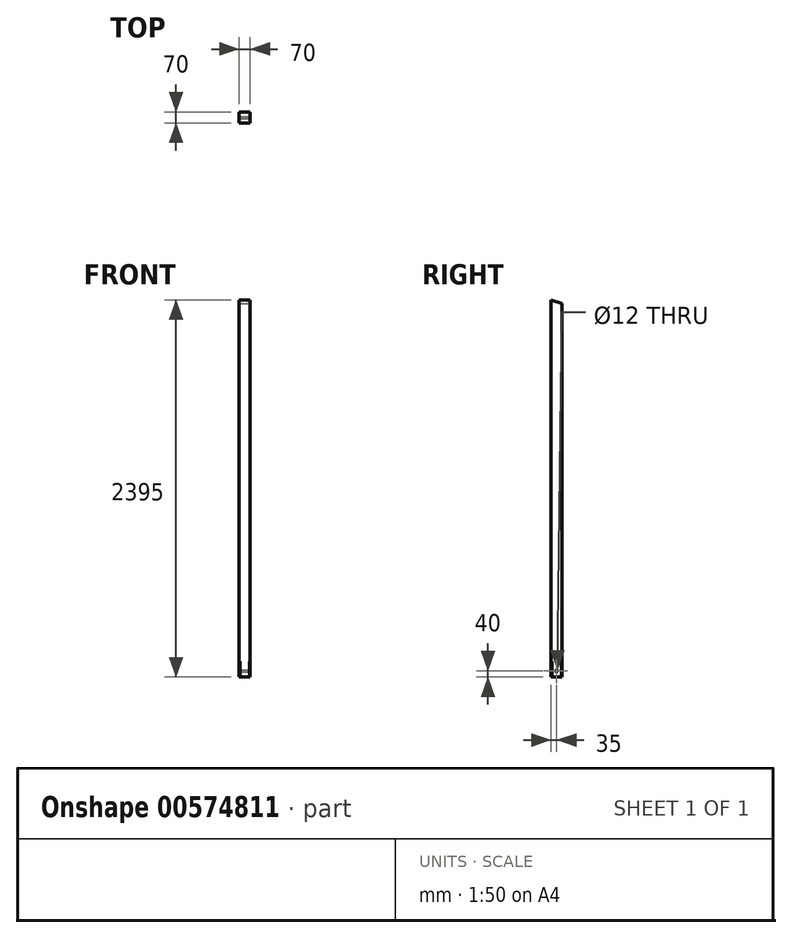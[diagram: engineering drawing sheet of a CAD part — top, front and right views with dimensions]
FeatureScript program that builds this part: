
annotation { "Feature Type Name" : "Feature", "Feature Type Description" : "" }
export const myFeature = defineFeature(function(context is Context, id is Id, definition is map)
    precondition{}
    {
        {
            var Q0;
            Q0=qCreatedBy(makeId("Top.planeOp"),FACE);
            var sketch = newSketch(context, id + "F0", { "sketchPlane" : qUnion([Q0])});
            skLineSegment(sketch, "E0.bottom", {"start": v(-35, -35) * mm, "end": v(35, -35) * mm});
            skLineSegment(sketch, "E0.top", {"start": v(-35, 35) * mm, "end": v(35, 35) * mm});
            skLineSegment(sketch, "E0.left", {"start": v(-35, -35) * mm, "end": v(-35, 35) * mm});
            skLineSegment(sketch, "E0.right", {"start": v(35, -35) * mm, "end": v(35, 35) * mm});
            skSolve(sketch);
        }
        {
            var Q0;
            Q0=makeQuery(id+"F0.imprint","IMPRINT",FACE,{"disambiguationData":[TD([[makeQuery(id+"F0.imprint","IMPRINT",EDGE,{"derivedFrom":sQuery(id+"F0.wireOp",EDGE,"E0.bottom")}),1.0]])]});
            extrude(context, id + "F1", {"entities" : qUnion([Q0]), "depth" : 100 * mm, "offsetDistance" : 25 * mm});
        }
        {
            var Q0;
            Q0=makeQuery(id+"F1.opExtrude","SWEPT_EDGE",EDGE,{"disambiguationData":[OSD([sQuery(id+"F0.wireOp",EDGE,"E0.bottom"),sQuery(id+"F0.wireOp",EDGE,"E0.left")])]});
            var Q1;
            Q1=makeQuery(id+"F1.opExtrude","SWEPT_EDGE",EDGE,{"disambiguationData":[OSD([sQuery(id+"F0.wireOp",EDGE,"E0.bottom"),sQuery(id+"F0.wireOp",EDGE,"E0.right")])]});
            var Q2;
            Q2=makeQuery(id+"F1.opExtrude","SWEPT_EDGE",EDGE,{"disambiguationData":[OSD([sQuery(id+"F0.wireOp",EDGE,"E0.top"),sQuery(id+"F0.wireOp",EDGE,"E0.right")])]});
            var Q3;
            Q3=makeQuery(id+"F1.opExtrude","SWEPT_EDGE",EDGE,{"disambiguationData":[OSD([sQuery(id+"F0.wireOp",EDGE,"E0.top"),sQuery(id+"F0.wireOp",EDGE,"E0.left")])]});
            chamfer(context, id + "F2", {"entities" : qUnion([Q0, Q1, Q2, Q3]), "width" : 5 * mm, "tangentPropagation" : true});
        }
        {
            var Q0;
            Q0=makeQuery(id+"F1.opExtrude","CAP_FACE",FACE,{"disambiguationData":[OSD([sQuery(id+"F0.wireOp",EDGE,"E0.bottom"),sQuery(id+"F0.wireOp",EDGE,"E0.top"),sQuery(id+"F0.wireOp",EDGE,"E0.left"),sQuery(id+"F0.wireOp",EDGE,"E0.right")])],"isStart":false});
            var sketch = newSketch(context, id + "F3", { "sketchPlane" : qUnion([Q0])});
            skLineSegment(sketch, "E1.bottom", {"start": v(35, 35) * mm, "end": v(-35, 35) * mm});
            skLineSegment(sketch, "E1.top", {"start": v(35, -35) * mm, "end": v(-35, -35) * mm});
            skLineSegment(sketch, "E1.left", {"start": v(35, 35) * mm, "end": v(35, -35) * mm});
            skLineSegment(sketch, "E1.right", {"start": v(-35, 35) * mm, "end": v(-35, -35) * mm});
            skSolve(sketch);
        }
        {
            var Q0;
            Q0=qSketchRegion(id+"F3",true);
            extrude(context, id + "F4", {"entities" : qUnion([Q0]), "operationType" : NewBodyOperationType.ADD, "depth" : 2295 * mm, "offsetDistance" : 25 * mm});
        }
        {
            var Q0;
            Q0=makeQuery(id+"F4.boolean.opBoolean","MERGE",FACE,{"derivedFrom":[makeQuery(id+"F1.opExtrude","SWEPT_FACE",FACE,{"disambiguationData":[OSD([sQuery(id+"F0.wireOp",EDGE,"E0.right")])]}),makeQuery(id+"F4.opExtrude","SWEPT_FACE",FACE,{"disambiguationData":[OSD([sQuery(id+"F3.wireOp",EDGE,"E1.left")])]})]});
            var sketch = newSketch(context, id + "F5", { "sketchPlane" : qUnion([Q0])});
            skCircle(sketch, "E2", {"center": v(0, 40) * mm, "radius": 6 * mm});
            skLineSegment(sketch, "E3", {"start": v(-35, 2395) * mm, "end": v(35, 2395) * mm});
            skLineSegment(sketch, "E4", {"start": v(35, 2395) * mm, "end": v(35, 2371.67) * mm});
            skLineSegment(sketch, "E5", {"start": v(35, 2371.67) * mm, "end": v(-35, 2395) * mm});
            skSolve(sketch);
        }
        {
            var Q0;
            Q0=qSketchRegion(id+"F5",true);
            extrude(context, id + "F6", {"entities" : qUnion([Q0]), "operationType" : NewBodyOperationType.REMOVE, "endBound" : BoundingType.THROUGH_ALL, "oppositeDirection" : true, "depth" : 25 * mm, "offsetDistance" : 25 * mm});
        }
    });
